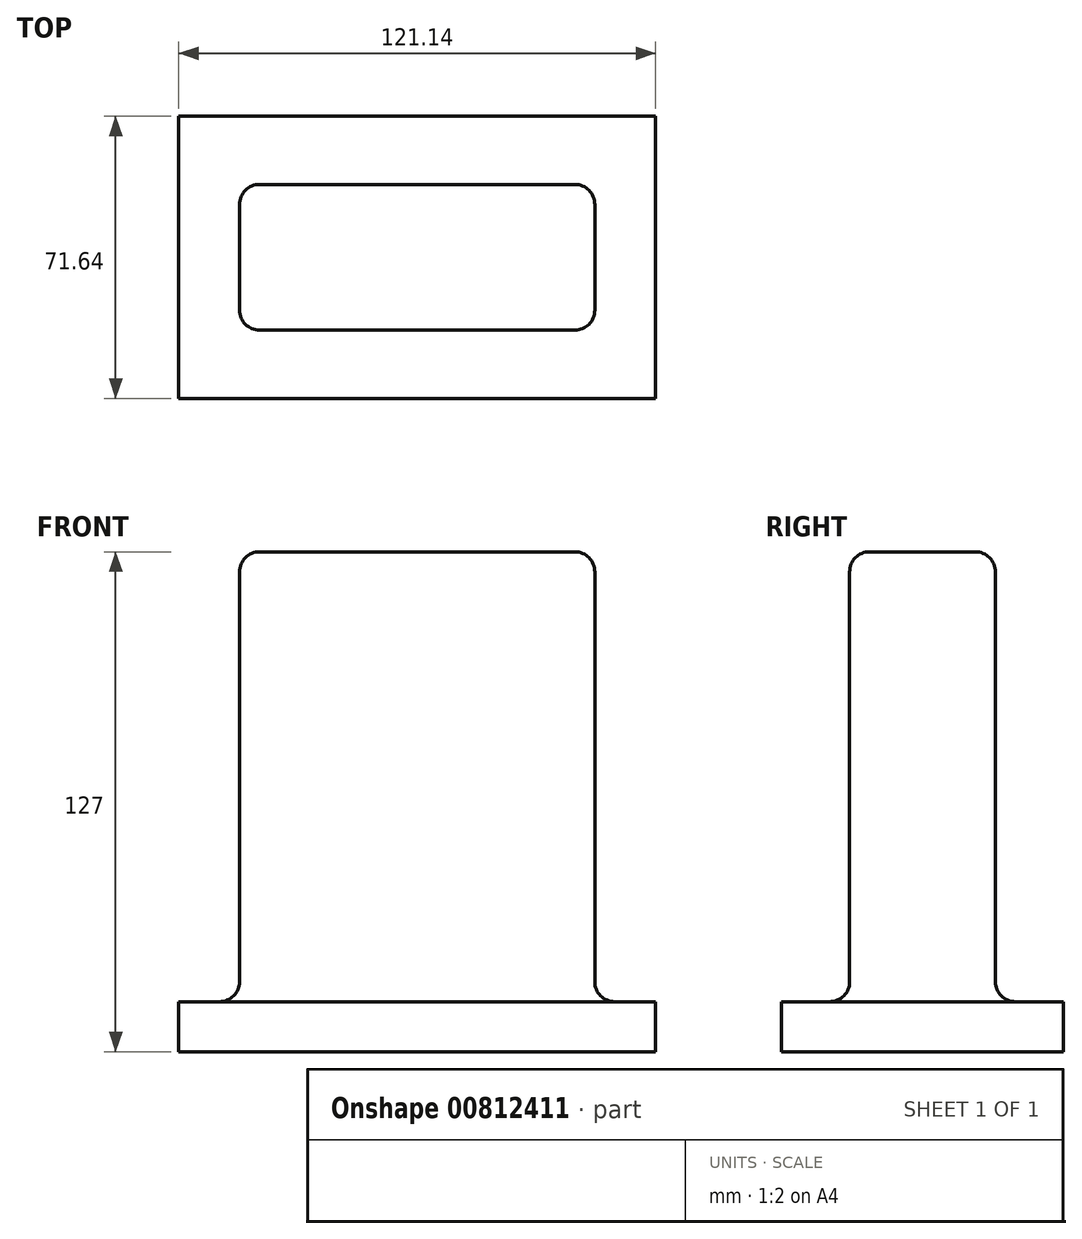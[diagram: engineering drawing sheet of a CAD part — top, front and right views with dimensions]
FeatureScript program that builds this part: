
annotation { "Feature Type Name" : "Feature", "Feature Type Description" : "" }
export const myFeature = defineFeature(function(context is Context, id is Id, definition is map)
    precondition{}
    {
        {
            var Q0;
            Q0=qCreatedBy(makeId("Top.planeOp"),FACE);
            var sketch = newSketch(context, id + "F0", { "sketchPlane" : qUnion([Q0])});
            skLineSegment(sketch, "E0.bottom", {"start": v(-60.57, -35.82) * mm, "end": v(60.57, -35.82) * mm});
            skLineSegment(sketch, "E0.top", {"start": v(-60.57, 35.82) * mm, "end": v(60.57, 35.82) * mm});
            skLineSegment(sketch, "E0.left", {"start": v(-60.57, -35.82) * mm, "end": v(-60.57, 35.82) * mm});
            skLineSegment(sketch, "E0.right", {"start": v(60.57, -35.82) * mm, "end": v(60.57, 35.82) * mm});
            skPoint(sketch, "E0.middle", {"position": v(0, 0) * mm});
            skSolve(sketch);
        }
        {
            var Q0;
            Q0=makeQuery(id+"F0.imprint","IMPRINT",FACE,{"disambiguationData":[TD([[makeQuery(id+"F0.imprint","IMPRINT",EDGE,{"derivedFrom":sQuery(id+"F0.wireOp",EDGE,"E0.bottom")}),1.0]])]});
            extrude(context, id + "F1", {"entities" : qUnion([Q0]), "depth" : 12.7 * mm, "offsetDistance" : 25.4 * mm});
        }
        {
            var Q0;
            Q0=qCreatedBy(makeId("Top.planeOp"),FACE);
            var sketch = newSketch(context, id + "F2", { "sketchPlane" : qUnion([Q0])});
            skLineSegment(sketch, "E1.bottom", {"start": v(-45.12, -18.51) * mm, "end": v(45.12, -18.51) * mm});
            skLineSegment(sketch, "E1.top", {"start": v(-45.12, 18.51) * mm, "end": v(45.12, 18.51) * mm});
            skLineSegment(sketch, "E1.left", {"start": v(-45.12, -18.51) * mm, "end": v(-45.12, 18.51) * mm});
            skLineSegment(sketch, "E1.right", {"start": v(45.12, -18.51) * mm, "end": v(45.12, 18.51) * mm});
            skPoint(sketch, "E1.middle", {"position": v(0, 0) * mm});
            skSolve(sketch);
        }
        {
            var Q0;
            Q0 = qSketchRegion(id + "F2", true);
            extrude(context, id + "F3", {"entities" : qUnion([Q0]), "operationType" : NewBodyOperationType.ADD, "depth" : 127 * mm, "offsetDistance" : 25.4 * mm});
        }
        {
            var Q0;
            Q0=makeQuery(id+"F3.opExtrude","SWEPT_FACE",FACE,{"disambiguationData":[OSD([sQuery(id+"F2.wireOp",EDGE,"E1.right")])]});
            fillet(context, id + "F4", {"entities" : qUnion([Q0]), "radius" : 5.08 * mm, "tangentPropagation" : true, "allowEdgeOverflow" : false});
        }
        {
            var Q0;
            Q0=makeQuery(id+"F3.opExtrude","SWEPT_FACE",FACE,{"disambiguationData":[OSD([sQuery(id+"F2.wireOp",EDGE,"E1.left")])]});
            fillet(context, id + "F5", {"entities" : qUnion([Q0]), "radius" : 5.08 * mm, "tangentPropagation" : true, "allowEdgeOverflow" : false});
        }
        {
            var Q0;
            Q0=makeQuery(id+"F3.opExtrude","SWEPT_FACE",FACE,{"disambiguationData":[OSD([sQuery(id+"F2.wireOp",EDGE,"E1.bottom")])]});
            var Q1;
            Q1=makeQuery(id+"F3.opExtrude","SWEPT_FACE",FACE,{"disambiguationData":[OSD([sQuery(id+"F2.wireOp",EDGE,"E1.top")])]});
            fillet(context, id + "F6", {"entities" : qUnion([Q0, Q1]), "radius" : 5.08 * mm, "tangentPropagation" : true, "allowEdgeOverflow" : false});
        }
    });
